# Revit family: HC_Boiler_MEPcontent_De Dietrich Thermique_Thermodynamic water heater TWH  E
name_source: partatom
category: Mechanical Equipment
revit_build: Autodesk Revit MEP 2015 (Build: 20151007_1515(x64)
units: mm (PartAtom-declared; Revit-internal decimal feet)

## types (2) — shared parameters
Angle = 60.00°
Angle 2 = 50.00°
Article Description = Water heater with heat pump
Black = Color RGB 045-045-045
Blue = Color RGB 002-061-157
Cap Diameter = 640 mm  [stored 2.09974 ft]
Cap Diameter Offset = 680 mm  [stored 2.23097 ft]
Cap Height = 400 mm
Cap Height Offset = 420 mm  [stored 1.37795 ft]
Content Supplier URL = www.mepcontent.eu
Custom = No
DCW Distance = 90 mm
Description = Water heater with heat pump
Diameter = 600 mm
Domestic Cold Water Diameter = 19 mm  [stored 0.062336 ft]
Domestic Hot Water Diameter = 19 mm  [stored 0.062336 ft]
Drain Diameter = 16 mm  [stored 0.0524934 ft]
Duct Distance 1 = 217 mm
EMCS Version = 3.0
ETIM Article Class = EC011396
Exhaust Air Diameter = 200 mm
Family Version = 10.24
Glass = Color RGB 218-227-224
Green = Color RGB 106-158-058
Grey = Color RAL 9006
IFCExportAs = IfcBoilerType
Length = 697 mm
Logo Distance = 145 mm
MEPcontent Class = BOILER
Manufacturer = De Dietrich Thermique
Manufacturer URL = http://www.dedietrich-thermique.fr
Pipe Type Category = M561
Power = 500 W
Product Line = De Dietrich Thermique
Radius = 318 mm
Red = Color RGB 198-000-000
Revit Version = 2015
Supply Air Diameter = 200 mm
URL = www.stabiplan.com
Use Nominal Diameter = Yes
Voltage = 230 V
White = Color RAL 9016
Width = 690 mm

## per-type parameters (varying)
| type | DHW Distance | Drain Distance | GTIN | H | Height | Height Service Area | Manufacturer Art. No. | Volume |
| 200 E | 974 mm | 1280 mm | 3661238496903 | 1270 mm | 1690 mm  [stored 5.54462 ft] | 1690 mm  [stored 5.54462 ft] | 100017408 | 215.0 L |
| 300 E | 1287 mm  [stored 4.22244 ft] | 1590 mm  [stored 5.21654 ft] | 3661238496880 | 1580 mm  [stored 5.18373 ft] | 2000 mm  [stored 6.56168 ft] | 2000 mm  [stored 6.56168 ft] | 100017410 | 270.0 L |

note: column(s) folded — value = type name in every type: Article Type, Model

note: [stored X ft] marks values corroborated as IEEE doubles in the binary element streams (Revit-internal decimal feet)

## geometry (parser evidence)
native form markers: Sweep x4
no freeform markers — native parametric forms only
